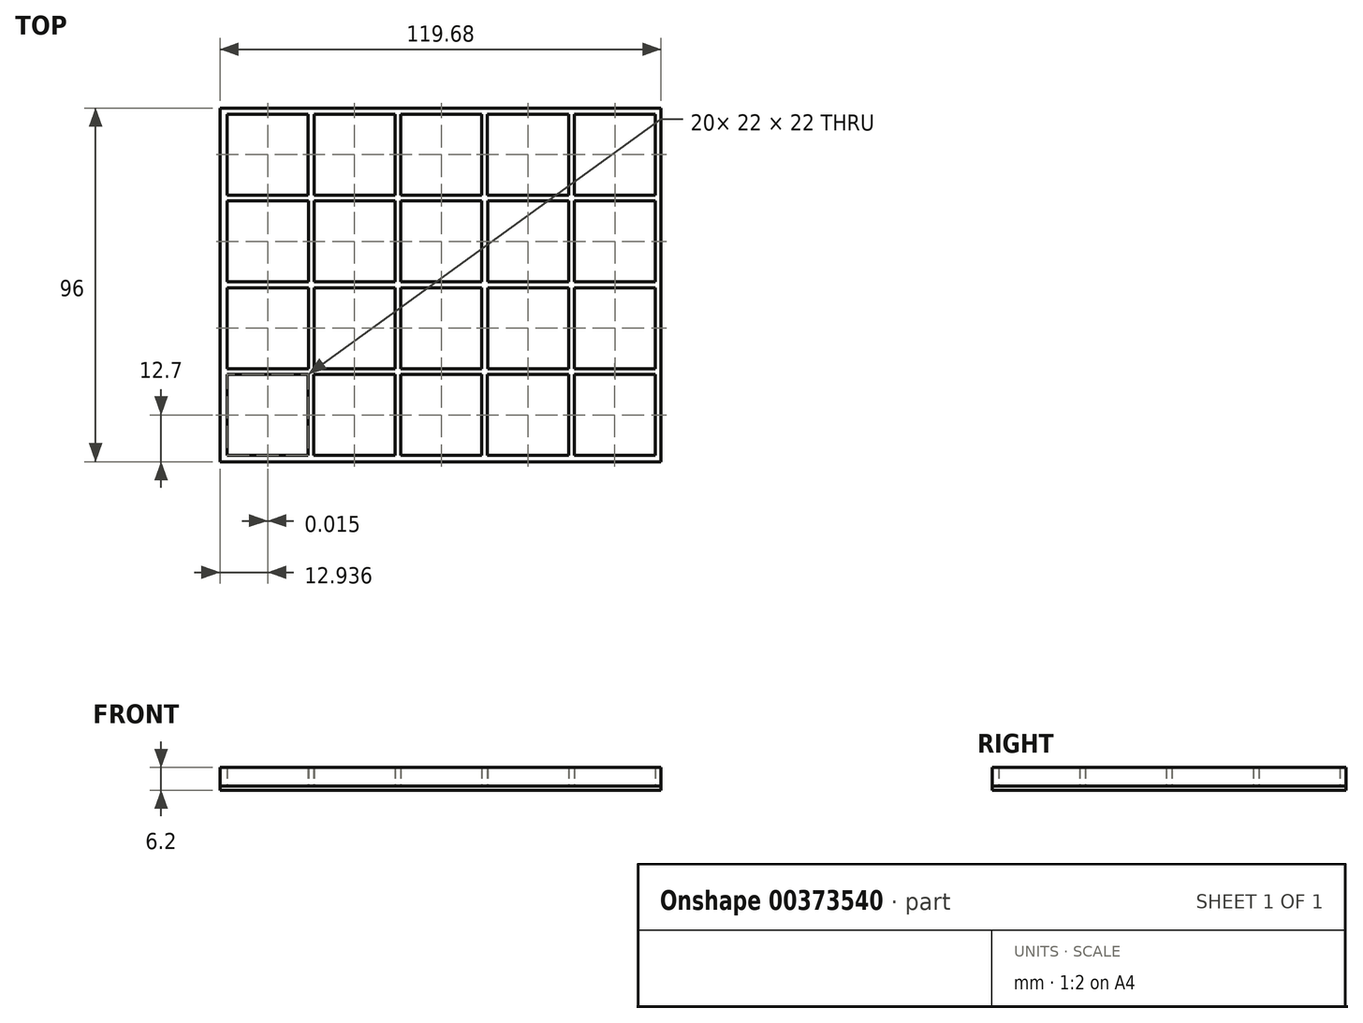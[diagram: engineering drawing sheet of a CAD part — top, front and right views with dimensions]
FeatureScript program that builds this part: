
annotation { "Feature Type Name" : "Feature", "Feature Type Description" : "" }
export const myFeature = defineFeature(function(context is Context, id is Id, definition is map)
    precondition{}
    {
        {
            var Q0;
            Q0=qCreatedBy(makeId("Top.planeOp"),FACE);
            var sketch = newSketch(context, id + "F0", { "sketchPlane" : qUnion([Q0])});
            skLineSegment(sketch, "E0.bottom", {"start": v(59.84, 48) * mm, "end": v(-59.84, 48) * mm});
            skLineSegment(sketch, "E0.top", {"start": v(59.84, -48) * mm, "end": v(-59.84, -48) * mm});
            skLineSegment(sketch, "E0.left", {"start": v(59.84, 48) * mm, "end": v(59.84, -48) * mm});
            skLineSegment(sketch, "E0.right", {"start": v(-59.84, 48) * mm, "end": v(-59.84, -48) * mm});
            skPoint(sketch, "E0.middle", {"position": v(0, 0) * mm});
            skLineSegment(sketch, "E1", {"start": v(-35.89, 24.35) * mm, "end": v(-57.89, 24.35) * mm});
            skLineSegment(sketch, "E2", {"start": v(-57.89, 24.35) * mm, "end": v(-57.89, 46.35) * mm});
            skLineSegment(sketch, "E3", {"start": v(-57.89, 46.35) * mm, "end": v(-35.89, 46.35) * mm});
            skLineSegment(sketch, "E4", {"start": v(-35.89, 46.35) * mm, "end": v(-35.89, 24.35) * mm});
            skLineSegment(sketch, "E5", {"start": v(-35.86, 0.8) * mm, "end": v(-57.86, 0.8) * mm});
            skLineSegment(sketch, "E6", {"start": v(-57.86, 0.8) * mm, "end": v(-57.86, 22.8) * mm});
            skLineSegment(sketch, "E7", {"start": v(-57.86, 22.8) * mm, "end": v(-35.86, 22.8) * mm});
            skLineSegment(sketch, "E8", {"start": v(-35.86, 22.8) * mm, "end": v(-35.86, 0.8) * mm});
            skLineSegment(sketch, "E9", {"start": v(-35.87, -22.75) * mm, "end": v(-57.87, -22.75) * mm});
            skLineSegment(sketch, "E10", {"start": v(-57.87, -22.75) * mm, "end": v(-57.87, -0.75) * mm});
            skLineSegment(sketch, "E11", {"start": v(-57.87, -0.75) * mm, "end": v(-35.87, -0.75) * mm});
            skLineSegment(sketch, "E12", {"start": v(-35.87, -0.75) * mm, "end": v(-35.87, -22.75) * mm});
            skLineSegment(sketch, "E13", {"start": v(-35.9, -46.3) * mm, "end": v(-57.9, -46.3) * mm});
            skLineSegment(sketch, "E14", {"start": v(-57.9, -46.3) * mm, "end": v(-57.9, -24.3) * mm});
            skLineSegment(sketch, "E15", {"start": v(-57.9, -24.3) * mm, "end": v(-35.9, -24.3) * mm});
            skLineSegment(sketch, "E16", {"start": v(-35.9, -24.3) * mm, "end": v(-35.9, -46.3) * mm});
            skLineSegment(sketch, "E17", {"start": v(-12.34, 24.35) * mm, "end": v(-34.34, 24.35) * mm});
            skLineSegment(sketch, "E18", {"start": v(-34.34, 24.35) * mm, "end": v(-34.34, 46.35) * mm});
            skLineSegment(sketch, "E19", {"start": v(-34.34, 46.35) * mm, "end": v(-12.34, 46.35) * mm});
            skLineSegment(sketch, "E20", {"start": v(-12.34, 46.35) * mm, "end": v(-12.34, 24.35) * mm});
            skLineSegment(sketch, "E21", {"start": v(-12.3, 0.8) * mm, "end": v(-34.3, 0.8) * mm});
            skLineSegment(sketch, "E22", {"start": v(-34.3, 0.8) * mm, "end": v(-34.3, 22.8) * mm});
            skLineSegment(sketch, "E23", {"start": v(-34.3, 22.8) * mm, "end": v(-12.3, 22.8) * mm});
            skLineSegment(sketch, "E24", {"start": v(-12.3, 22.8) * mm, "end": v(-12.3, 0.8) * mm});
            skLineSegment(sketch, "E25", {"start": v(-12.32, -22.75) * mm, "end": v(-34.32, -22.75) * mm});
            skLineSegment(sketch, "E26", {"start": v(-34.32, -22.75) * mm, "end": v(-34.32, -0.75) * mm});
            skLineSegment(sketch, "E27", {"start": v(-34.32, -0.75) * mm, "end": v(-12.32, -0.75) * mm});
            skLineSegment(sketch, "E28", {"start": v(-12.32, -0.75) * mm, "end": v(-12.32, -22.75) * mm});
            skLineSegment(sketch, "E29", {"start": v(-12.35, -46.3) * mm, "end": v(-34.35, -46.3) * mm});
            skLineSegment(sketch, "E30", {"start": v(-34.35, -46.3) * mm, "end": v(-34.35, -24.3) * mm});
            skLineSegment(sketch, "E31", {"start": v(-34.35, -24.3) * mm, "end": v(-12.35, -24.3) * mm});
            skLineSegment(sketch, "E32", {"start": v(-12.35, -24.3) * mm, "end": v(-12.35, -46.3) * mm});
            skLineSegment(sketch, "E33", {"start": v(11.21, 24.35) * mm, "end": v(-10.79, 24.35) * mm});
            skLineSegment(sketch, "E34", {"start": v(-10.79, 24.35) * mm, "end": v(-10.79, 46.35) * mm});
            skLineSegment(sketch, "E35", {"start": v(-10.79, 46.35) * mm, "end": v(11.21, 46.35) * mm});
            skLineSegment(sketch, "E36", {"start": v(11.21, 46.35) * mm, "end": v(11.21, 24.35) * mm});
            skLineSegment(sketch, "E37", {"start": v(11.24, 0.8) * mm, "end": v(-10.76, 0.8) * mm});
            skLineSegment(sketch, "E38", {"start": v(-10.76, 0.8) * mm, "end": v(-10.76, 22.8) * mm});
            skLineSegment(sketch, "E39", {"start": v(-10.76, 22.8) * mm, "end": v(11.24, 22.8) * mm});
            skLineSegment(sketch, "E40", {"start": v(11.24, 22.8) * mm, "end": v(11.24, 0.8) * mm});
            skLineSegment(sketch, "E41", {"start": v(11.23, -22.75) * mm, "end": v(-10.77, -22.75) * mm});
            skLineSegment(sketch, "E42", {"start": v(-10.77, -22.75) * mm, "end": v(-10.77, -0.75) * mm});
            skLineSegment(sketch, "E43", {"start": v(-10.77, -0.75) * mm, "end": v(11.23, -0.75) * mm});
            skLineSegment(sketch, "E44", {"start": v(11.23, -0.75) * mm, "end": v(11.23, -22.75) * mm});
            skLineSegment(sketch, "E45", {"start": v(11.2, -46.3) * mm, "end": v(-10.8, -46.3) * mm});
            skLineSegment(sketch, "E46", {"start": v(-10.8, -46.3) * mm, "end": v(-10.8, -24.3) * mm});
            skLineSegment(sketch, "E47", {"start": v(-10.8, -24.3) * mm, "end": v(11.2, -24.3) * mm});
            skLineSegment(sketch, "E48", {"start": v(11.2, -24.3) * mm, "end": v(11.2, -46.3) * mm});
            skLineSegment(sketch, "E49", {"start": v(34.76, 24.35) * mm, "end": v(12.76, 24.35) * mm});
            skLineSegment(sketch, "E50", {"start": v(12.76, 24.35) * mm, "end": v(12.76, 46.35) * mm});
            skLineSegment(sketch, "E51", {"start": v(12.76, 46.35) * mm, "end": v(34.76, 46.35) * mm});
            skLineSegment(sketch, "E52", {"start": v(34.76, 46.35) * mm, "end": v(34.76, 24.35) * mm});
            skLineSegment(sketch, "E53", {"start": v(34.8, 0.8) * mm, "end": v(12.8, 0.8) * mm});
            skLineSegment(sketch, "E54", {"start": v(12.8, 0.8) * mm, "end": v(12.8, 22.8) * mm});
            skLineSegment(sketch, "E55", {"start": v(12.8, 22.8) * mm, "end": v(34.8, 22.8) * mm});
            skLineSegment(sketch, "E56", {"start": v(34.8, 22.8) * mm, "end": v(34.8, 0.8) * mm});
            skLineSegment(sketch, "E57", {"start": v(34.78, -22.75) * mm, "end": v(12.78, -22.75) * mm});
            skLineSegment(sketch, "E58", {"start": v(12.78, -22.75) * mm, "end": v(12.78, -0.75) * mm});
            skLineSegment(sketch, "E59", {"start": v(12.78, -0.75) * mm, "end": v(34.78, -0.75) * mm});
            skLineSegment(sketch, "E60", {"start": v(34.78, -0.75) * mm, "end": v(34.78, -22.75) * mm});
            skLineSegment(sketch, "E61", {"start": v(34.75, -46.3) * mm, "end": v(12.75, -46.3) * mm});
            skLineSegment(sketch, "E62", {"start": v(12.75, -46.3) * mm, "end": v(12.75, -24.3) * mm});
            skLineSegment(sketch, "E63", {"start": v(12.75, -24.3) * mm, "end": v(34.75, -24.3) * mm});
            skLineSegment(sketch, "E64", {"start": v(34.75, -24.3) * mm, "end": v(34.75, -46.3) * mm});
            skLineSegment(sketch, "E65", {"start": v(58.31, 24.35) * mm, "end": v(36.31, 24.35) * mm});
            skLineSegment(sketch, "E66", {"start": v(36.31, 24.35) * mm, "end": v(36.31, 46.35) * mm});
            skLineSegment(sketch, "E67", {"start": v(36.31, 46.35) * mm, "end": v(58.31, 46.35) * mm});
            skLineSegment(sketch, "E68", {"start": v(58.31, 46.35) * mm, "end": v(58.31, 24.35) * mm});
            skLineSegment(sketch, "E69", {"start": v(58.34, 0.8) * mm, "end": v(36.34, 0.8) * mm});
            skLineSegment(sketch, "E70", {"start": v(36.34, 0.8) * mm, "end": v(36.34, 22.8) * mm});
            skLineSegment(sketch, "E71", {"start": v(36.34, 22.8) * mm, "end": v(58.34, 22.8) * mm});
            skLineSegment(sketch, "E72", {"start": v(58.34, 22.8) * mm, "end": v(58.34, 0.8) * mm});
            skLineSegment(sketch, "E73", {"start": v(58.33, -22.75) * mm, "end": v(36.33, -22.75) * mm});
            skLineSegment(sketch, "E74", {"start": v(36.33, -22.75) * mm, "end": v(36.33, -0.75) * mm});
            skLineSegment(sketch, "E75", {"start": v(36.33, -0.75) * mm, "end": v(58.33, -0.75) * mm});
            skLineSegment(sketch, "E76", {"start": v(58.33, -0.75) * mm, "end": v(58.33, -22.75) * mm});
            skLineSegment(sketch, "E77", {"start": v(58.3, -46.3) * mm, "end": v(36.3, -46.3) * mm});
            skLineSegment(sketch, "E78", {"start": v(36.3, -46.3) * mm, "end": v(36.3, -24.3) * mm});
            skLineSegment(sketch, "E79", {"start": v(36.3, -24.3) * mm, "end": v(58.3, -24.3) * mm});
            skLineSegment(sketch, "E80", {"start": v(58.3, -24.3) * mm, "end": v(58.3, -46.3) * mm});
            skSolve(sketch);
        }
        {
            var Q0;
            Q0=makeQuery(id+"F0.imprint","IMPRINT",FACE,{"disambiguationData":[TD([[makeQuery(id+"F0.imprint","IMPRINT",EDGE,{"derivedFrom":sQuery(id+"F0.wireOp",EDGE,"E65")}),-1.0]])]});
            var Q1;
            Q1=makeQuery(id+"F0.imprint","IMPRINT",FACE,{"disambiguationData":[TD([[makeQuery(id+"F0.imprint","IMPRINT",EDGE,{"derivedFrom":sQuery(id+"F0.wireOp",EDGE,"E69")}),-1.0]])]});
            var Q2;
            Q2=makeQuery(id+"F0.imprint","IMPRINT",FACE,{"disambiguationData":[TD([[makeQuery(id+"F0.imprint","IMPRINT",EDGE,{"derivedFrom":sQuery(id+"F0.wireOp",EDGE,"E61")}),-1.0]])]});
            var Q3;
            Q3=makeQuery(id+"F0.imprint","IMPRINT",FACE,{"disambiguationData":[TD([[makeQuery(id+"F0.imprint","IMPRINT",EDGE,{"derivedFrom":sQuery(id+"F0.wireOp",EDGE,"E53")}),-1.0]])]});
            var Q4;
            Q4=makeQuery(id+"F0.imprint","IMPRINT",FACE,{"disambiguationData":[TD([[makeQuery(id+"F0.imprint","IMPRINT",EDGE,{"derivedFrom":sQuery(id+"F0.wireOp",EDGE,"E57")}),-1.0]])]});
            var Q5;
            Q5=makeQuery(id+"F0.imprint","IMPRINT",FACE,{"disambiguationData":[TD([[makeQuery(id+"F0.imprint","IMPRINT",EDGE,{"derivedFrom":sQuery(id+"F0.wireOp",EDGE,"E13")}),-1.0]])]});
            var Q6;
            Q6=makeQuery(id+"F0.imprint","IMPRINT",FACE,{"disambiguationData":[TD([[makeQuery(id+"F0.imprint","IMPRINT",EDGE,{"derivedFrom":sQuery(id+"F0.wireOp",EDGE,"E17")}),-1.0]])]});
            var Q7;
            Q7=makeQuery(id+"F0.imprint","IMPRINT",FACE,{"disambiguationData":[TD([[makeQuery(id+"F0.imprint","IMPRINT",EDGE,{"derivedFrom":sQuery(id+"F0.wireOp",EDGE,"E21")}),-1.0]])]});
            var Q8;
            Q8=makeQuery(id+"F0.imprint","IMPRINT",FACE,{"disambiguationData":[TD([[makeQuery(id+"F0.imprint","IMPRINT",EDGE,{"derivedFrom":sQuery(id+"F0.wireOp",EDGE,"E25")}),-1.0]])]});
            var Q9;
            Q9=makeQuery(id+"F0.imprint","IMPRINT",FACE,{"disambiguationData":[TD([[makeQuery(id+"F0.imprint","IMPRINT",EDGE,{"derivedFrom":sQuery(id+"F0.wireOp",EDGE,"E29")}),-1.0]])]});
            var Q10;
            Q10=makeQuery(id+"F0.imprint","IMPRINT",FACE,{"disambiguationData":[TD([[makeQuery(id+"F0.imprint","IMPRINT",EDGE,{"derivedFrom":sQuery(id+"F0.wireOp",EDGE,"E33")}),-1.0]])]});
            var Q11;
            Q11=makeQuery(id+"F0.imprint","IMPRINT",FACE,{"disambiguationData":[TD([[makeQuery(id+"F0.imprint","IMPRINT",EDGE,{"derivedFrom":sQuery(id+"F0.wireOp",EDGE,"E37")}),-1.0]])]});
            var Q12;
            Q12=makeQuery(id+"F0.imprint","IMPRINT",FACE,{"disambiguationData":[TD([[makeQuery(id+"F0.imprint","IMPRINT",EDGE,{"derivedFrom":sQuery(id+"F0.wireOp",EDGE,"E41")}),-1.0]])]});
            var Q13;
            Q13=makeQuery(id+"F0.imprint","IMPRINT",FACE,{"disambiguationData":[TD([[makeQuery(id+"F0.imprint","IMPRINT",EDGE,{"derivedFrom":sQuery(id+"F0.wireOp",EDGE,"E45")}),-1.0]])]});
            var Q14;
            Q14=makeQuery(id+"F0.imprint","IMPRINT",FACE,{"disambiguationData":[TD([[makeQuery(id+"F0.imprint","IMPRINT",EDGE,{"derivedFrom":sQuery(id+"F0.wireOp",EDGE,"E49")}),-1.0]])]});
            var Q15;
            Q15=makeQuery(id+"F0.imprint","IMPRINT",FACE,{"disambiguationData":[TD([[makeQuery(id+"F0.imprint","IMPRINT",EDGE,{"derivedFrom":sQuery(id+"F0.wireOp",EDGE,"E73")}),-1.0]])]});
            var Q16;
            Q16=makeQuery(id+"F0.imprint","IMPRINT",FACE,{"disambiguationData":[TD([[makeQuery(id+"F0.imprint","IMPRINT",EDGE,{"derivedFrom":sQuery(id+"F0.wireOp",EDGE,"E77")}),-1.0]])]});
            var Q17;
            Q17=makeQuery(id+"F0.imprint","IMPRINT",FACE,{"disambiguationData":[TD([[makeQuery(id+"F0.imprint","IMPRINT",EDGE,{"derivedFrom":sQuery(id+"F0.wireOp",EDGE,"E0.bottom")}),1.0]])]});
            var Q18;
            Q18=makeQuery(id+"F0.imprint","IMPRINT",FACE,{"disambiguationData":[TD([[makeQuery(id+"F0.imprint","IMPRINT",EDGE,{"derivedFrom":sQuery(id+"F0.wireOp",EDGE,"E1")}),-1.0]])]});
            var Q19;
            Q19=makeQuery(id+"F0.imprint","IMPRINT",FACE,{"disambiguationData":[TD([[makeQuery(id+"F0.imprint","IMPRINT",EDGE,{"derivedFrom":sQuery(id+"F0.wireOp",EDGE,"E5")}),-1.0]])]});
            var Q20;
            Q20=makeQuery(id+"F0.imprint","IMPRINT",FACE,{"disambiguationData":[TD([[makeQuery(id+"F0.imprint","IMPRINT",EDGE,{"derivedFrom":sQuery(id+"F0.wireOp",EDGE,"E9")}),-1.0]])]});
            extrude(context, id + "F1", {"entities" : qUnion([Q0, Q1, Q2, Q3, Q4, Q5, Q6, Q7, Q8, Q9, Q10, Q11, Q12, Q13, Q14, Q15, Q16, Q17, Q18, Q19, Q20]), "oppositeDirection" : true, "depth" : 1.2 * mm});
        }
        {
            var Q0;
            Q0=makeQuery(id+"F0.imprint","IMPRINT",FACE,{"disambiguationData":[TD([[makeQuery(id+"F0.imprint","IMPRINT",EDGE,{"derivedFrom":sQuery(id+"F0.wireOp",EDGE,"E0.bottom")}),1.0]])]});
            extrude(context, id + "F2", {"entities" : qUnion([Q0]), "depth" : 5 * mm});
        }
    });
